# Revit family: Geräteeinsätze GES_Geräteeinsatz_GES6_mit_Griffbügel
name_source: partatom
category: Generic Models
revit_build: Autodesk Revit 2015 (Build: 20140606_1530(x64)
units: mm (PartAtom-declared; Revit-internal decimal feet)

## types (3) — shared parameters
Height = 61 mm  [stored 0.200131 ft]
Inner cut = 16 mm  [stored 0.0524934 ft]
Inner cut2 = 16 mm  [stored 0.0524934 ft]
Manufacturer = OBO Bettermann
Snur width = 88 mm
URL = http://www.obo-bettermann.com
Width = 273 mm  [stored 0.895669 ft]
Width 2 = 199 mm  [stored 0.652887 ft]

## per-type parameters (varying)
| type | GTIN | Manufacturer Art. No. | Material |
| GES6 U 9011 | 4012195103110 | 7405312 | Plastic RAL 9011 |
| GES6 U 7011 | 4012195103080
4012196460540 | 7405308 | Plastic RAL 7011 |
| GES6 U 1019 | 4012195103127 | 7405316 | Plastic RAL 1019 |

note: column(s) folded — value = type name in every type: Article Type

note: [stored X ft] marks values corroborated as IEEE doubles in the binary element streams (Revit-internal decimal feet)

## geometry (parser evidence)
native form markers: Sweep x2
no freeform markers — native parametric forms only
